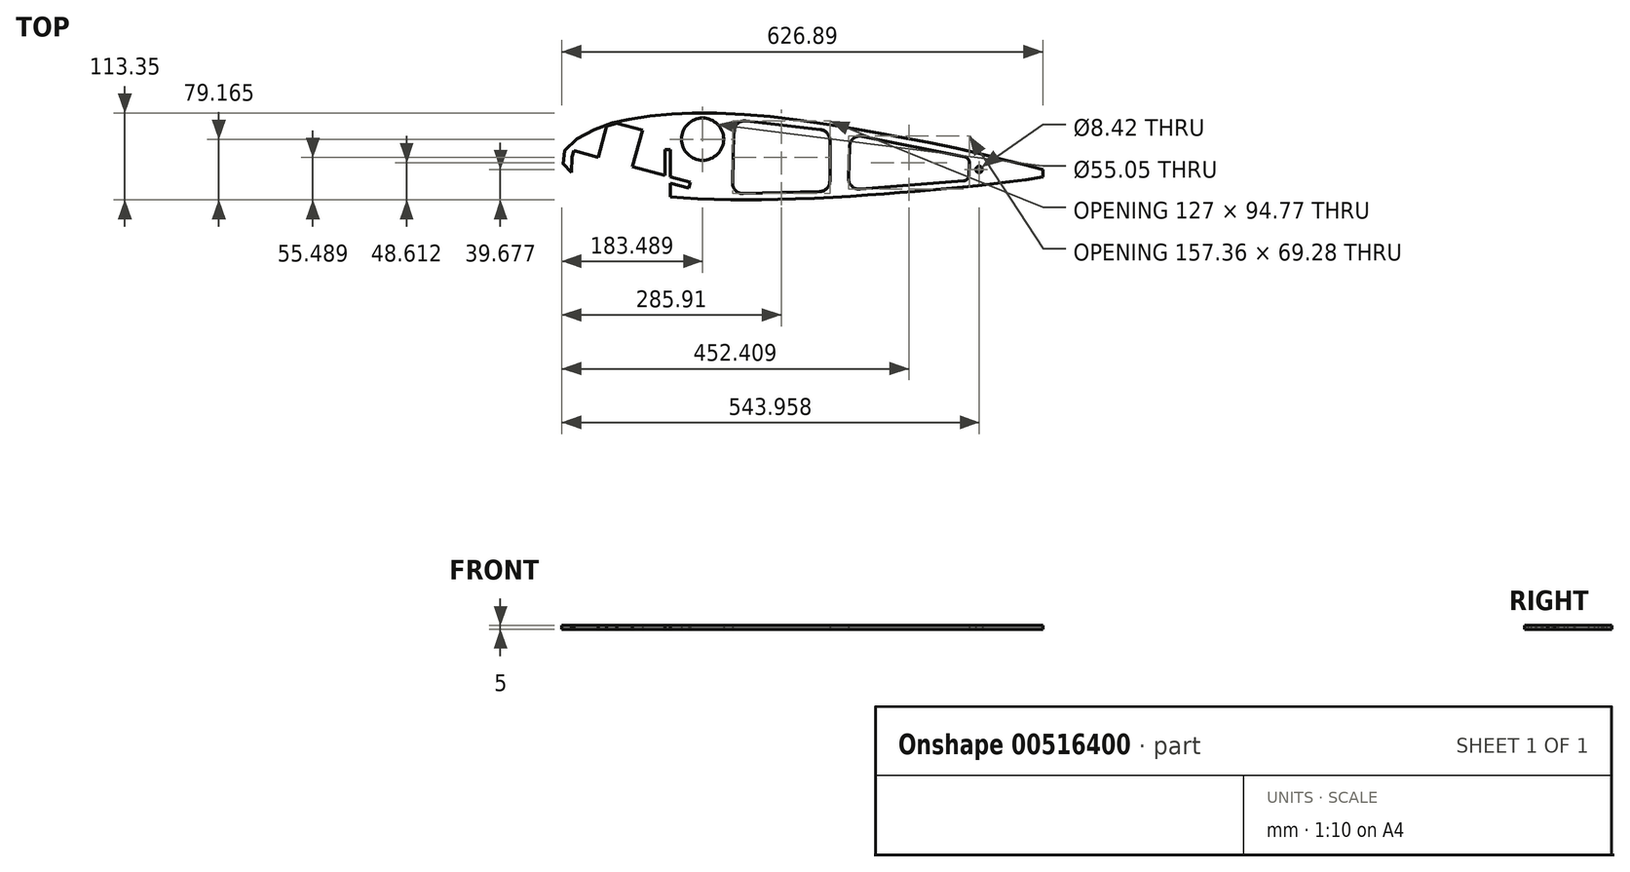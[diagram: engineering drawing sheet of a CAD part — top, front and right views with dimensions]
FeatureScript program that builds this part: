
annotation { "Feature Type Name" : "Feature", "Feature Type Description" : "" }
export const myFeature = defineFeature(function(context is Context, id is Id, definition is map)
    precondition{}
    {
        {
            var Q0;
            Q0=qCreatedBy(makeId("Top.planeOp"),FACE);
            var sketch = newSketch(context, id + "F0", { "sketchPlane" : qUnion([Q0])});
            skFitSpline(sketch, "E0", {"points": [v(518.68, -926.4) * mm, v(505.04, -917.22) * mm, v(497.96, -902.43) * mm, v(507.88, -885.28) * mm, v(537.93, -866.24) * mm, v(573.97, -854.6) * mm, v(633.6, -846.1) * mm, v(679.56, -844.37) * mm, v(748.01, -847.51) * mm, v(826.53, -857.11) * mm, v(958.09, -879.62) * mm, v(1042.6, -898.03) * mm, v(1118.02, -917.54) * mm], "startDerivative": vector(-292.83, 162.03) * mm, "endDerivative": vector(739.06, -196.15) * mm});
            skLineSegment(sketch, "E1", {"start": v(1118.02, -917.54) * mm, "end": v(1117.65, -927.32) * mm});
            skFitSpline(sketch, "E2", {"points": [v(1117.65, -927.32) * mm, v(1080.37, -932.32) * mm, v(988.42, -942.24) * mm, v(858.71, -951.9) * mm, v(778.25, -955.83) * mm, v(700.93, -956.09) * mm, v(638.9, -952.28) * mm], "startDerivative": vector(-289.5, -40.43) * mm, "endDerivative": vector(-483.4, 63.83) * mm});
            skLineSegment(sketch, "E3", {"start": v(638.9, -952.28) * mm, "end": v(638.9, -932.62) * mm});
            skLineSegment(sketch, "E4", {"start": v(638.9, -932.62) * mm, "end": v(671.92, -941.86) * mm});
            skLineSegment(sketch, "E5", {"start": v(671.92, -941.86) * mm, "end": v(674.14, -933.9) * mm});
            skLineSegment(sketch, "E6", {"start": v(674.14, -933.9) * mm, "end": v(638.9, -924.04) * mm});
            skLineSegment(sketch, "E7", {"start": v(638.9, -924.04) * mm, "end": v(638.9, -891.53) * mm});
            skLineSegment(sketch, "E8", {"start": v(638.9, -891.53) * mm, "end": v(631.95, -891.53) * mm});
            skLineSegment(sketch, "E9", {"start": v(631.95, -891.53) * mm, "end": v(631.95, -922.09) * mm});
            skLineSegment(sketch, "E10", {"start": v(631.95, -922.09) * mm, "end": v(598.6, -913) * mm});
            skLineSegment(sketch, "E11", {"start": v(598.6, -913) * mm, "end": v(611.62, -865.26) * mm});
            skLineSegment(sketch, "E12", {"start": v(611.62, -865.26) * mm, "end": v(575.4, -855.39) * mm});
            skLineSegment(sketch, "E13", {"start": v(575.4, -855.39) * mm, "end": v(567.31, -857.46) * mm});
            skLineSegment(sketch, "E14", {"start": v(567.31, -857.46) * mm, "end": v(555.39, -901.23) * mm});
            skLineSegment(sketch, "E15", {"start": v(555.39, -901.23) * mm, "end": v(522.39, -892.24) * mm});
            skLineSegment(sketch, "E16", {"start": v(522.39, -892.24) * mm, "end": v(518.68, -905.87) * mm});
            skLineSegment(sketch, "E17", {"start": v(518.68, -905.87) * mm, "end": v(518.68, -926.4) * mm});
            skCircle(sketch, "E18", {"center": v(679.66, -877.81) * mm, "radius": 26.35 * mm});
            skCircle(sketch, "E19", {"center": v(700.64, -934.18) * mm, "radius": 4.85 * mm});
            skCircle(sketch, "E20", {"center": v(1025.1, -916.13) * mm, "radius": 4.06 * mm});
            skCircle(sketch, "E21", {"center": v(857.75, -918.36) * mm, "radius": 4.89 * mm});
            skLineSegment(sketch, "E22", {"start": v(740.76, -853.78) * mm, "end": v(826.02, -863.51) * mm});
            skLineSegment(sketch, "E23", {"start": v(838.43, -877.42) * mm, "end": v(838.43, -933.12) * mm});
            skLineSegment(sketch, "E24", {"start": v(824.9, -947.1) * mm, "end": v(737.72, -950.06) * mm});
            skLineSegment(sketch, "E25", {"start": v(723.25, -935.68) * mm, "end": v(725.18, -867.3) * mm});
            skPoint(sketch, "E26.visualSharp", {"position": v(725.6, -852.05) * mm});
            skArc(sketch, "E26.filletArc", {"start": v(740.76, -853.78) * mm, "mid": v(730, -857.11) * mm, "end": v(725.18, -867.3) * mm});
            skPoint(sketch, "E27.visualSharp", {"position": v(838.43, -864.93) * mm});
            skArc(sketch, "E27.filletArc", {"start": v(838.43, -877.42) * mm, "mid": v(834.88, -868.1) * mm, "end": v(826.02, -863.51) * mm});
            skPoint(sketch, "E28.visualSharp", {"position": v(838.43, -946.65) * mm});
            skArc(sketch, "E28.filletArc", {"start": v(824.9, -947.1) * mm, "mid": v(834.5, -942.85) * mm, "end": v(838.43, -933.12) * mm});
            skPoint(sketch, "E29.visualSharp", {"position": v(722.83, -950.57) * mm});
            skArc(sketch, "E29.filletArc", {"start": v(723.25, -935.68) * mm, "mid": v(727.37, -946) * mm, "end": v(737.72, -950.06) * mm});
            skLineSegment(sketch, "E30", {"start": v(889.03, -873.9) * mm, "end": v(993.32, -894.08) * mm});
            skLineSegment(sketch, "E31", {"start": v(1004.66, -907.83) * mm, "end": v(1004.66, -921.01) * mm});
            skLineSegment(sketch, "E32", {"start": v(991.79, -934.96) * mm, "end": v(886.28, -943.5) * mm});
            skPoint(sketch, "E33.visualSharp", {"position": v(1004.66, -896.27) * mm});
            skArc(sketch, "E33.filletArc", {"start": v(1004.66, -907.83) * mm, "mid": v(1001.46, -898.92) * mm, "end": v(993.32, -894.08) * mm});
            skPoint(sketch, "E34.visualSharp", {"position": v(1004.66, -933.92) * mm});
            skArc(sketch, "E34.filletArc", {"start": v(991.79, -934.96) * mm, "mid": v(1000.95, -930.5) * mm, "end": v(1004.66, -921.01) * mm});
            skLineSegment(sketch, "E35", {"start": v(873.56, -904.5) * mm, "end": v(873.56, -887.37) * mm});
            skFitSpline(sketch, "E36", {"points": [v(889.03, -873.9) * mm, v(881.45, -875.17) * mm, v(876.27, -879.24) * mm, v(873.56, -887.37) * mm], "startDerivative": vector(-34.23, 1.49) * mm, "endDerivative": vector(-2.74, -31.94) * mm});
            skFitSpline(sketch, "E37", {"points": [v(873.56, -904.5) * mm, v(875.8, -908.39) * mm, v(877.96, -912.5) * mm, v(878.9, -917.56) * mm, v(878.24, -924.39) * mm, v(876.09, -928.97) * mm, v(874.22, -931.97) * mm, v(874.4, -935.7) * mm, v(877.3, -939.83) * mm, v(880.86, -942.26) * mm, v(886.28, -943.5) * mm], "startDerivative": vector(22.84, -40.06) * mm, "endDerivative": vector(53.73, -8.44) * mm});
            skLineSegment(sketch, "E38", {"start": v(922.52, -783.64) * mm, "end": v(921.84, -803.96) * mm});
            skFitSpline(sketch, "E39", {"points": [v(921.84, -803.96) * mm, v(913.18, -795.86) * mm, v(909.15, -784.7) * mm, v(917.72, -768.74) * mm, v(938.23, -753.94) * mm, v(967.82, -741.35) * mm, v(989.24, -735.64) * mm, v(1021.17, -730.32) * mm, v(1057.77, -727.07) * mm, v(1092.3, -726.03) * mm, v(1150.06, -728.24) * mm, v(1201.6, -733.43) * mm, v(1268.18, -742.78) * mm, v(1319.26, -751.5) * mm, v(1372.01, -761.65) * mm, v(1425.42, -772.73) * mm, v(1473.03, -783.94) * mm, v(1508.6, -792.82) * mm, v(1536, -800.1) * mm], "startDerivative": vector(-290.04, 231.78) * mm, "endDerivative": vector(539.02, -145.24) * mm});
            skLineSegment(sketch, "E40", {"start": v(1536, -800.1) * mm, "end": v(1536, -809.5) * mm});
            skFitSpline(sketch, "E41", {"points": [v(1536, -809.5) * mm, v(1492.64, -816.03) * mm, v(1454.52, -820.3) * mm, v(1415.57, -824.37) * mm, v(1376.26, -827.8) * mm, v(1339.9, -830.53) * mm, v(1298.7, -833.68) * mm, v(1250.08, -836.49) * mm, v(1197.04, -838.66) * mm, v(1156.82, -839.36) * mm, v(1118.64, -839.08) * mm, v(1078.14, -837.47) * mm, v(1050.6, -835.23) * mm], "startDerivative": vector(-507.75, -81.32) * mm, "endDerivative": vector(-377.64, 34.85) * mm});
            skLineSegment(sketch, "E42", {"start": v(1050.6, -835.23) * mm, "end": v(1050.6, -817.87) * mm});
            skLineSegment(sketch, "E43", {"start": v(1050.6, -817.87) * mm, "end": v(1074.57, -824.16) * mm});
            skLineSegment(sketch, "E44", {"start": v(1074.57, -824.16) * mm, "end": v(1076.68, -816.17) * mm});
            skLineSegment(sketch, "E45", {"start": v(1076.68, -816.17) * mm, "end": v(1050.6, -809.32) * mm});
            skLineSegment(sketch, "E46", {"start": v(1050.6, -809.32) * mm, "end": v(1050.6, -774) * mm});
            skLineSegment(sketch, "E47", {"start": v(1050.6, -774) * mm, "end": v(1043.68, -774) * mm});
            skLineSegment(sketch, "E48", {"start": v(1043.68, -774) * mm, "end": v(1043.68, -807.8) * mm});
            skLineSegment(sketch, "E49", {"start": v(1043.68, -807.8) * mm, "end": v(1001.1, -796.23) * mm});
            skLineSegment(sketch, "E50", {"start": v(1001.1, -796.23) * mm, "end": v(1014.1, -748.33) * mm});
            skLineSegment(sketch, "E51", {"start": v(1014.1, -748.33) * mm, "end": v(980.74, -739.27) * mm});
            skLineSegment(sketch, "E52", {"start": v(980.74, -739.27) * mm, "end": v(967.47, -743.28) * mm});
            skLineSegment(sketch, "E53", {"start": v(967.47, -743.28) * mm, "end": v(956.71, -783.83) * mm});
            skLineSegment(sketch, "E54", {"start": v(956.71, -783.83) * mm, "end": v(924.95, -775.4) * mm});
            skLineSegment(sketch, "E55", {"start": v(924.95, -775.4) * mm, "end": v(922.52, -783.64) * mm});
            skCircle(sketch, "E56", {"center": v(1092.6, -760.21) * mm, "radius": 27.52 * mm});
            skCircle(sketch, "E57", {"center": v(1453.08, -799.7) * mm, "radius": 4.21 * mm});
            skLineSegment(sketch, "E58", {"start": v(1133.17, -750.1) * mm, "end": v(1131.53, -816.94) * mm});
            skLineSegment(sketch, "E59", {"start": v(1148.76, -736.53) * mm, "end": v(1246.12, -747.68) * mm});
            skLineSegment(sketch, "E60", {"start": v(1258.53, -761.6) * mm, "end": v(1258.53, -814.72) * mm});
            skLineSegment(sketch, "E61", {"start": v(1244.89, -828.72) * mm, "end": v(1145.89, -831.28) * mm});
            skPoint(sketch, "E62.visualSharp", {"position": v(1133.54, -734.8) * mm});
            skArc(sketch, "E62.filletArc", {"start": v(1148.76, -736.53) * mm, "mid": v(1137.97, -739.88) * mm, "end": v(1133.17, -750.1) * mm});
            skPoint(sketch, "E63.visualSharp", {"position": v(1258.53, -749.1) * mm});
            skArc(sketch, "E63.filletArc", {"start": v(1258.53, -761.6) * mm, "mid": v(1254.98, -752.27) * mm, "end": v(1246.12, -747.68) * mm});
            skPoint(sketch, "E64.visualSharp", {"position": v(1258.53, -828.37) * mm});
            skArc(sketch, "E64.filletArc", {"start": v(1244.89, -828.72) * mm, "mid": v(1254.55, -824.5) * mm, "end": v(1258.53, -814.72) * mm});
            skPoint(sketch, "E65.visualSharp", {"position": v(1131.17, -831.66) * mm});
            skArc(sketch, "E65.filletArc", {"start": v(1131.53, -816.94) * mm, "mid": v(1135.63, -827.19) * mm, "end": v(1145.89, -831.28) * mm});
            skLineSegment(sketch, "E66", {"start": v(1284.17, -769.68) * mm, "end": v(1282.85, -811) * mm});
            skLineSegment(sketch, "E67", {"start": v(1297.96, -825.4) * mm, "end": v(1433.1, -814.6) * mm});
            skLineSegment(sketch, "E68", {"start": v(1439.54, -807.88) * mm, "end": v(1440.2, -790.47) * mm});
            skLineSegment(sketch, "E69", {"start": v(1434.6, -783.33) * mm, "end": v(1300.92, -756.4) * mm});
            skPoint(sketch, "E70.visualSharp", {"position": v(1284.7, -753.13) * mm});
            skArc(sketch, "E70.filletArc", {"start": v(1300.92, -756.4) * mm, "mid": v(1289.46, -759.15) * mm, "end": v(1284.17, -769.68) * mm});
            skPoint(sketch, "E71.visualSharp", {"position": v(1282.35, -826.66) * mm});
            skArc(sketch, "E71.filletArc", {"start": v(1282.85, -811) * mm, "mid": v(1287.18, -821.59) * mm, "end": v(1297.96, -825.4) * mm});
            skPoint(sketch, "E72.visualSharp", {"position": v(1440.44, -784.51) * mm});
            skArc(sketch, "E72.filletArc", {"start": v(1440.2, -790.47) * mm, "mid": v(1438.72, -785.87) * mm, "end": v(1434.6, -783.33) * mm});
            skPoint(sketch, "E73.visualSharp", {"position": v(1439.3, -814.1) * mm});
            skArc(sketch, "E73.filletArc", {"start": v(1433.1, -814.6) * mm, "mid": v(1437.6, -812.46) * mm, "end": v(1439.54, -807.88) * mm});
            skLineSegment(sketch, "E74", {"start": v(1018.55, -1020.71) * mm, "end": v(1018.55, -970.67) * mm});
            skFitSpline(sketch, "E75", {"points": [v(1018.55, -970.67) * mm, v(1025.26, -966.89) * mm, v(1036.61, -962.5) * mm, v(1052.6, -957.74) * mm, v(1072.25, -953.46) * mm, v(1089.95, -950.78) * mm, v(1109.23, -948.95) * mm, v(1130.59, -947.6) * mm, v(1139.62, -947.24) * mm], "startDerivative": vector(69.98, 43.05) * mm, "endDerivative": vector(82.35, 2.82) * mm});
            skLineSegment(sketch, "E76", {"start": v(1139.62, -947.24) * mm, "end": v(1139.62, -954.07) * mm});
            skLineSegment(sketch, "E77", {"start": v(1139.62, -954.07) * mm, "end": v(1160.24, -954.07) * mm});
            skLineSegment(sketch, "E78", {"start": v(1160.24, -954.07) * mm, "end": v(1160.24, -947.24) * mm});
            skFitSpline(sketch, "E79", {"points": [v(1160.24, -947.24) * mm, v(1173.06, -947.24) * mm, v(1188.8, -948.1) * mm, v(1207.1, -949.56) * mm, v(1223.7, -951.15) * mm, v(1244.33, -953.59) * mm, v(1261.79, -955.9) * mm, v(1281.31, -958.83) * mm], "startDerivative": vector(102.15, 1.36) * mm, "endDerivative": vector(130.9, -20.09) * mm});
            skLineSegment(sketch, "E80", {"start": v(1281.31, -958.83) * mm, "end": v(1280.37, -965.44) * mm});
            skLineSegment(sketch, "E81", {"start": v(1280.37, -965.44) * mm, "end": v(1300.74, -968.34) * mm});
            skLineSegment(sketch, "E82", {"start": v(1300.74, -968.34) * mm, "end": v(1301.62, -962.14) * mm});
            skFitSpline(sketch, "E83", {"points": [v(1301.62, -962.14) * mm, v(1313.57, -963.98) * mm, v(1339.38, -968.6) * mm, v(1378.97, -975.92) * mm, v(1419.03, -984.08) * mm, v(1460.32, -993.02) * mm, v(1493.83, -1001.5) * mm, v(1521.33, -1008.66) * mm], "startDerivative": vector(123.07, -17.94) * mm, "endDerivative": vector(197.8, -51.39) * mm});
            skLineSegment(sketch, "E84", {"start": v(1521.33, -1008.66) * mm, "end": v(1521.06, -1018.5) * mm});
            skFitSpline(sketch, "E85", {"points": [v(1521.06, -1018.5) * mm, v(1501.18, -1021.48) * mm, v(1474.19, -1024.7) * mm, v(1413.03, -1031.15) * mm, v(1356.2, -1035.77) * mm, v(1325.38, -1037.83) * mm, v(1301.67, -1039.3) * mm], "startDerivative": vector(-155.84, -24.47) * mm, "endDerivative": vector(-170.23, -10.33) * mm});
            skLineSegment(sketch, "E86", {"start": v(1301.67, -1039.3) * mm, "end": v(1301.67, -1032.73) * mm});
            skLineSegment(sketch, "E87", {"start": v(1301.67, -1032.73) * mm, "end": v(1280.88, -1033.7) * mm});
            skLineSegment(sketch, "E88", {"start": v(1280.88, -1033.7) * mm, "end": v(1281.2, -1040.36) * mm});
            skFitSpline(sketch, "E89", {"points": [v(1281.2, -1040.36) * mm, v(1252.52, -1041.47) * mm, v(1221.88, -1042.5) * mm, v(1190.2, -1042.62) * mm, v(1160.56, -1042.06) * mm], "startDerivative": vector(-116.89, -4.47) * mm, "endDerivative": vector(-119.36, 4.55) * mm});
            skLineSegment(sketch, "E90", {"start": v(1160.56, -1042.06) * mm, "end": v(1160.56, -1035.41) * mm});
            skLineSegment(sketch, "E91", {"start": v(1160.56, -1035.41) * mm, "end": v(1140.2, -1034.59) * mm});
            skLineSegment(sketch, "E92", {"start": v(1140.2, -1034.59) * mm, "end": v(1140.2, -1040.91) * mm});
            skFitSpline(sketch, "E93", {"points": [v(1018.55, -1020.71) * mm, v(1027.41, -1024.43) * mm, v(1040.7, -1028.38) * mm, v(1059.12, -1032.33) * mm, v(1076.54, -1035.03) * mm, v(1097.56, -1037.72) * mm, v(1118.84, -1039.88) * mm, v(1140.2, -1040.91) * mm], "startDerivative": vector(79.74, -35.85) * mm, "endDerivative": vector(135.23, -4.92) * mm});
            skCircle(sketch, "E94", {"center": v(1435.97, -1008.12) * mm, "radius": 4.12 * mm});
            skLineSegment(sketch, "E95", {"start": v(1358.7, -979.06) * mm, "end": v(1405.99, -988.36) * mm});
            skLineSegment(sketch, "E96", {"start": v(1411.64, -995.23) * mm, "end": v(1411.64, -1017.99) * mm});
            skLineSegment(sketch, "E97", {"start": v(1405.15, -1024.97) * mm, "end": v(1357.6, -1028.45) * mm});
            skLineSegment(sketch, "E98", {"start": v(1350.08, -1021.42) * mm, "end": v(1350.35, -985.87) * mm});
            skPoint(sketch, "E99.visualSharp", {"position": v(1350.41, -977.43) * mm});
            skArc(sketch, "E99.filletArc", {"start": v(1358.7, -979.06) * mm, "mid": v(1352.92, -980.5) * mm, "end": v(1350.35, -985.87) * mm});
            skPoint(sketch, "E100.visualSharp", {"position": v(1411.64, -989.47) * mm});
            skArc(sketch, "E100.filletArc", {"start": v(1411.64, -995.23) * mm, "mid": v(1410.04, -990.78) * mm, "end": v(1405.99, -988.36) * mm});
            skPoint(sketch, "E101.visualSharp", {"position": v(1411.64, -1024.5) * mm});
            skArc(sketch, "E101.filletArc", {"start": v(1405.15, -1024.97) * mm, "mid": v(1409.76, -1022.75) * mm, "end": v(1411.64, -1017.99) * mm});
            skPoint(sketch, "E102.visualSharp", {"position": v(1350.03, -1029) * mm});
            skArc(sketch, "E102.filletArc", {"start": v(1350.08, -1021.42) * mm, "mid": v(1352.3, -1026.58) * mm, "end": v(1357.6, -1028.45) * mm});
            skLineSegment(sketch, "E103", {"start": v(1178.83, -955.03) * mm, "end": v(1259.58, -962.64) * mm});
            skLineSegment(sketch, "E104", {"start": v(1277.7, -982.62) * mm, "end": v(1277.6, -1014.57) * mm});
            skLineSegment(sketch, "E105", {"start": v(1257.95, -1034.5) * mm, "end": v(1177.85, -1035.91) * mm});
            skLineSegment(sketch, "E106", {"start": v(1157.5, -1016.18) * mm, "end": v(1156.96, -975.2) * mm});
            skPoint(sketch, "E107.visualSharp", {"position": v(1156.66, -952.94) * mm});
            skArc(sketch, "E107.filletArc", {"start": v(1178.83, -955.03) * mm, "mid": v(1163.4, -960.24) * mm, "end": v(1156.96, -975.2) * mm});
            skPoint(sketch, "E108.visualSharp", {"position": v(1277.77, -964.35) * mm});
            skArc(sketch, "E108.filletArc", {"start": v(1277.7, -982.62) * mm, "mid": v(1272.52, -969.11) * mm, "end": v(1259.58, -962.64) * mm});
            skPoint(sketch, "E109.visualSharp", {"position": v(1277.53, -1034.15) * mm});
            skArc(sketch, "E109.filletArc", {"start": v(1257.95, -1034.5) * mm, "mid": v(1271.84, -1028.54) * mm, "end": v(1277.6, -1014.57) * mm});
            skPoint(sketch, "E110.visualSharp", {"position": v(1157.77, -1036.27) * mm});
            skArc(sketch, "E110.filletArc", {"start": v(1157.5, -1016.18) * mm, "mid": v(1163.58, -1030.27) * mm, "end": v(1177.85, -1035.91) * mm});
            skLineSegment(sketch, "E111", {"start": v(1143.09, -975.14) * mm, "end": v(1143.02, -1013.08) * mm});
            skLineSegment(sketch, "E112", {"start": v(1032.21, -1013.58) * mm, "end": v(1031.98, -976.73) * mm});
            skPoint(sketch, "E113.visualSharp", {"position": v(1143.13, -951.23) * mm});
            skArc(sketch, "E113.filletArc", {"start": v(1143.09, -975.14) * mm, "mid": v(1135.94, -959.78) * mm, "end": v(1119.57, -955.41) * mm});
            skPoint(sketch, "E114.visualSharp", {"position": v(1142.98, -1036.28) * mm});
            skArc(sketch, "E114.filletArc", {"start": v(1120.04, -1032.82) * mm, "mid": v(1136.06, -1028.21) * mm, "end": v(1143.02, -1013.08) * mm});
            skPoint(sketch, "E115.visualSharp", {"position": v(1031.95, -970.82) * mm});
            skArc(sketch, "E115.filletArc", {"start": v(1037.77, -969.8) * mm, "mid": v(1033.6, -972.2) * mm, "end": v(1031.98, -976.73) * mm});
            skPoint(sketch, "E116.visualSharp", {"position": v(1032.25, -1019.57) * mm});
            skArc(sketch, "E116.filletArc", {"start": v(1032.21, -1013.58) * mm, "mid": v(1033.92, -1018.12) * mm, "end": v(1038.17, -1020.46) * mm});
            skFitSpline(sketch, "E117", {"points": [v(1037.77, -969.8) * mm, v(1049.96, -965.7) * mm, v(1071.1, -960.97) * mm, v(1094.44, -957.16) * mm, v(1119.57, -955.41) * mm], "startDerivative": vector(57, 21) * mm, "endDerivative": vector(94.03, 2.23) * mm});
            skFitSpline(sketch, "E118", {"points": [v(1038.17, -1020.46) * mm, v(1056.13, -1024.64) * mm, v(1073.84, -1027.78) * mm, v(1096.97, -1030.79) * mm, v(1120.04, -1032.82) * mm], "startDerivative": vector(76.81, -18.77) * mm, "endDerivative": vector(86.3, -6.77) * mm});
            skLineSegment(sketch, "E119", {"start": v(717.3, -1035.03) * mm, "end": v(717.3, -1109.05) * mm});
            skLineSegment(sketch, "E120", {"start": v(915.69, -1033.19) * mm, "end": v(915.69, -1118.62) * mm});
            skLineSegment(sketch, "E121", {"start": v(951.18, -1031.75) * mm, "end": v(950.3, -1038.24) * mm});
            skLineSegment(sketch, "E122", {"start": v(950.3, -1038.24) * mm, "end": v(970.6, -1041.02) * mm});
            skLineSegment(sketch, "E123", {"start": v(970.6, -1041.02) * mm, "end": v(971.4, -1035.14) * mm});
            skLineSegment(sketch, "E124", {"start": v(971.67, -1116.14) * mm, "end": v(971.33, -1109.55) * mm});
            skLineSegment(sketch, "E125", {"start": v(971.33, -1109.55) * mm, "end": v(951.23, -1110.6) * mm});
            skLineSegment(sketch, "E126", {"start": v(951.23, -1110.6) * mm, "end": v(951.58, -1117.22) * mm});
            skLineSegment(sketch, "E127", {"start": v(669.77, -1044.94) * mm, "end": v(669.77, -1096.36) * mm});
            skLineSegment(sketch, "E128", {"start": v(1007.61, -1056.5) * mm, "end": v(1007.61, -1099.68) * mm});
            skLineSegment(sketch, "E129", {"start": v(1015.16, -1106.66) * mm, "end": v(1067.1, -1102.58) * mm});
            skLineSegment(sketch, "E130", {"start": v(1073.55, -1095.6) * mm, "end": v(1073.55, -1066.47) * mm});
            skLineSegment(sketch, "E131", {"start": v(1067.87, -1059.6) * mm, "end": v(1015.93, -1049.62) * mm});
            skPoint(sketch, "E132.visualSharp", {"position": v(1007.61, -1048.03) * mm});
            skArc(sketch, "E132.filletArc", {"start": v(1015.93, -1049.62) * mm, "mid": v(1010.15, -1051.1) * mm, "end": v(1007.61, -1056.5) * mm});
            skPoint(sketch, "E133.visualSharp", {"position": v(1073.55, -1060.69) * mm});
            skArc(sketch, "E133.filletArc", {"start": v(1073.55, -1066.47) * mm, "mid": v(1071.95, -1062.01) * mm, "end": v(1067.87, -1059.6) * mm});
            skPoint(sketch, "E134.visualSharp", {"position": v(1073.55, -1102.07) * mm});
            skArc(sketch, "E134.filletArc", {"start": v(1067.1, -1102.58) * mm, "mid": v(1071.7, -1100.35) * mm, "end": v(1073.55, -1095.6) * mm});
            skPoint(sketch, "E135.visualSharp", {"position": v(1007.61, -1107.25) * mm});
            skArc(sketch, "E135.filletArc", {"start": v(1007.61, -1099.68) * mm, "mid": v(1009.86, -1104.82) * mm, "end": v(1015.16, -1106.66) * mm});
            skFitSpline(sketch, "E136", {"points": [v(669.77, -1096.36) * mm, v(680.88, -1100.92) * mm, v(691.83, -1104.33) * mm, v(704.43, -1107.43) * mm, v(717.3, -1109.05) * mm], "startDerivative": vector(45.18, -19.6) * mm, "endDerivative": vector(50.21, -4.9) * mm});
            skFitSpline(sketch, "E137", {"points": [v(669.77, -1044.94) * mm, v(683.18, -1038.31) * mm, v(703.85, -1031.16) * mm, v(729.35, -1025.48) * mm, v(753.55, -1021.95) * mm, v(784.56, -1019.19) * mm, v(812.8, -1018.41) * mm, v(834.43, -1018.93) * mm, v(862.94, -1020.74) * mm, v(897.3, -1024.01) * mm, v(925.99, -1027.72) * mm, v(951.18, -1031.75) * mm], "startDerivative": vector(182.71, 97.06) * mm, "endDerivative": vector(275.5, -45.87) * mm});
            skFitSpline(sketch, "E138", {"points": [v(971.4, -1035.14) * mm, v(996.33, -1039.11) * mm, v(1029.81, -1044.94) * mm, v(1051.83, -1049.05) * mm, v(1086.6, -1055.93) * mm], "startDerivative": vector(100.52, -15.59) * mm, "endDerivative": vector(135.36, -27) * mm});
            skLineSegment(sketch, "E139", {"start": v(1086.6, -1055.93) * mm, "end": v(1086.6, -1107.5) * mm});
            skFitSpline(sketch, "E140", {"points": [v(1086.6, -1107.5) * mm, v(1047.1, -1110.95) * mm, v(1008.78, -1113.91) * mm, v(971.67, -1116.14) * mm], "startDerivative": vector(-117, -10.4) * mm, "endDerivative": vector(-112.82, -6.3) * mm});
            skFitSpline(sketch, "E141", {"points": [v(951.58, -1117.22) * mm, v(934.17, -1118.37) * mm, v(915.69, -1118.62) * mm], "startDerivative": vector(-35.05, -2.79) * mm, "endDerivative": vector(-36.7, -0.02) * mm});
            skFitSpline(sketch, "E142", {"points": [v(915.69, -1033.19) * mm, v(890.85, -1030.24) * mm, v(860.45, -1027.62) * mm, v(831, -1025.83) * mm, v(802.64, -1025.47) * mm, v(774.27, -1026.78) * mm, v(744.95, -1029.88) * mm, v(717.3, -1035.03) * mm], "startDerivative": vector(-180.2, 22.85) * mm, "endDerivative": vector(-192.67, -39.55) * mm});
            skFitSpline(sketch, "E143", {"points": [v(1112.15, -1061.66) * mm, v(1135.46, -1066.94) * mm, v(1166.1, -1074.43) * mm, v(1185.68, -1079.37) * mm, v(1203.12, -1084.22) * mm], "startDerivative": vector(87, -19.19) * mm, "endDerivative": vector(79.2, -22.52) * mm});
            skFitSpline(sketch, "E144", {"points": [v(1202.44, -1093.83) * mm, v(1178.61, -1097.58) * mm, v(1158.1, -1100.22) * mm, v(1134.87, -1102.85) * mm, v(1112.06, -1105.15) * mm], "startDerivative": vector(-94.8, -15.49) * mm, "endDerivative": vector(-90.17, -8.81) * mm});
            skLineSegment(sketch, "E145", {"start": v(1112.15, -1061.66) * mm, "end": v(1112.06, -1105.15) * mm});
            skLineSegment(sketch, "E146", {"start": v(1203.12, -1084.22) * mm, "end": v(1202.44, -1093.83) * mm});
            skLineSegment(sketch, "E147", {"start": v(1442.36, -931.5) * mm, "end": v(1442.36, -973.55) * mm});
            skLineSegment(sketch, "E148", {"start": v(1531.38, -953.17) * mm, "end": v(1530.92, -963.13) * mm});
            skFitSpline(sketch, "E149", {"points": [v(1442.36, -931.5) * mm, v(1461.9, -935.78) * mm, v(1486.82, -941.73) * mm, v(1507.85, -947.22) * mm, v(1531.38, -953.17) * mm], "startDerivative": vector(80.2, -17.23) * mm, "endDerivative": vector(93.5, -23.35) * mm});
            skFitSpline(sketch, "E150", {"points": [v(1530.92, -963.13) * mm, v(1510.27, -966.3) * mm, v(1491.47, -968.62) * mm, v(1468.31, -971.32) * mm, v(1442.36, -973.55) * mm], "startDerivative": vector(-86.75, -13.93) * mm, "endDerivative": vector(-96.62, -7.53) * mm});
            skSolve(sketch);
        }
        {
            var Q0;
            Q0=makeQuery(id+"F0.imprint","IMPRINT",FACE,{"disambiguationData":[TD([[makeQuery(id+"F0.imprint","IMPRINT",EDGE,{"derivedFrom":sQuery(id+"F0.wireOp",EDGE,"E38")}),-1.0]])]});
            extrude(context, id + "F1", {"entities" : qUnion([Q0]), "endBound" : BoundingType.SYMMETRIC, "depth" : 5 * mm, "offsetDistance" : 25 * mm});
        }
    });
